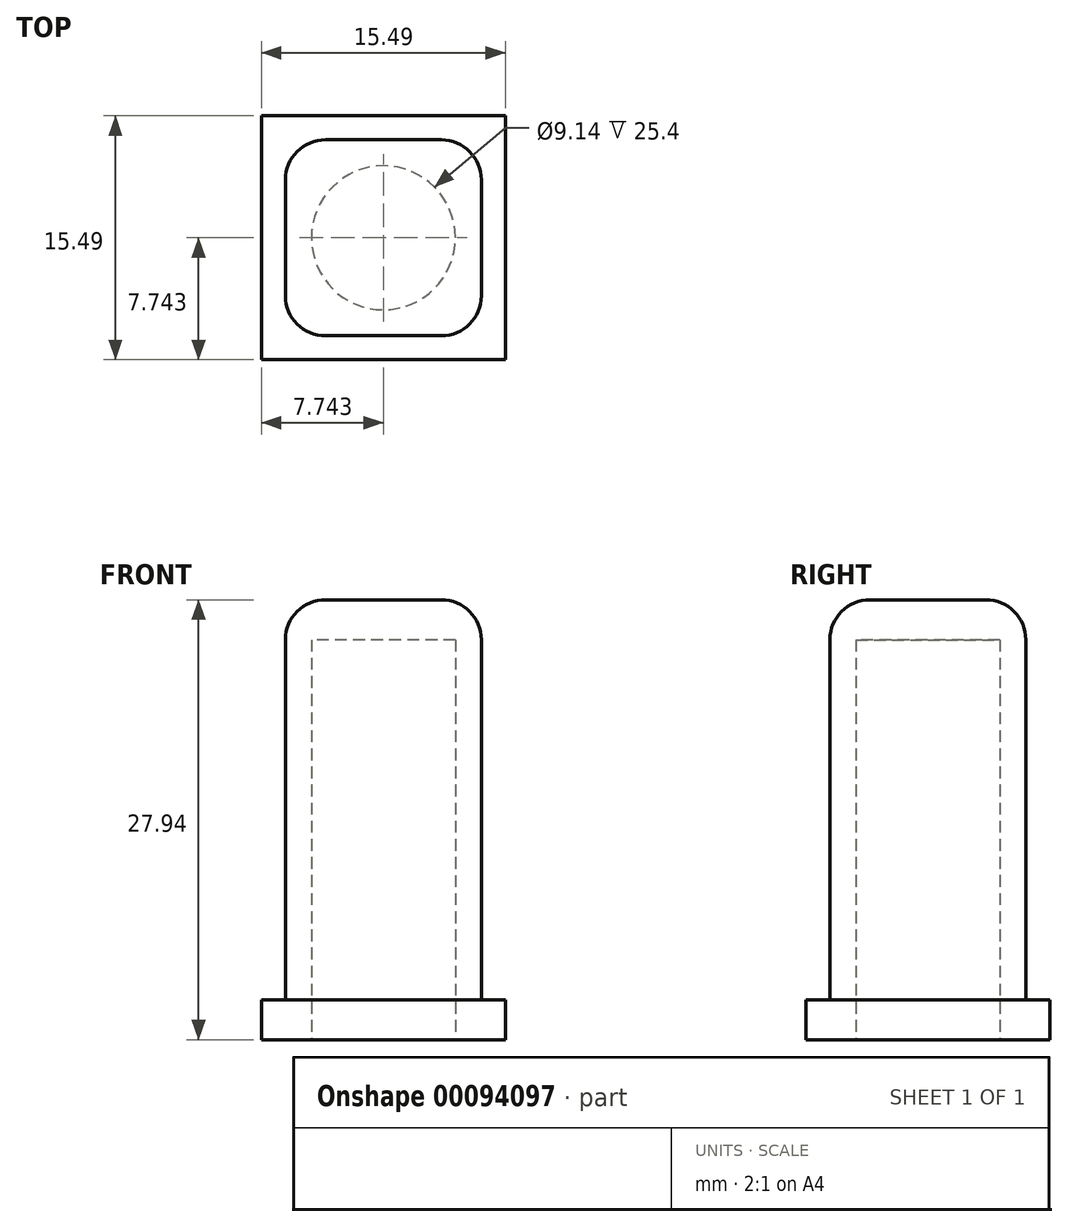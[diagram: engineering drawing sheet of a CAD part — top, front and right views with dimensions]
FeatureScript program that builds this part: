
annotation { "Feature Type Name" : "Feature", "Feature Type Description" : "" }
export const myFeature = defineFeature(function(context is Context, id is Id, definition is map)
    precondition{}
    {
        {
            var Q0;
            Q0=qCreatedBy(makeId("Top.planeOp"),FACE);
            var sketch = newSketch(context, id + "F0", { "sketchPlane" : qUnion([Q0])});
            skLineSegment(sketch, "E0.bottom", {"start": v(0, 0) * mm, "end": v(12.45, 0) * mm});
            skLineSegment(sketch, "E0.top", {"start": v(0, 12.45) * mm, "end": v(12.45, 12.45) * mm});
            skLineSegment(sketch, "E0.left", {"start": v(0, 0) * mm, "end": v(0, 12.45) * mm});
            skLineSegment(sketch, "E0.right", {"start": v(12.45, 0) * mm, "end": v(12.45, 12.45) * mm});
            skLineSegment(sketch, "E1", {"start": v(6.22, 12.45) * mm, "end": v(6.22, 0) * mm, "construction": true});
            skLineSegment(sketch, "E2", {"start": v(6.22, 0) * mm, "end": v(12.45, 6.22) * mm, "construction": true});
            skLineSegment(sketch, "E3", {"start": v(12.45, 6.22) * mm, "end": v(0, 6.22) * mm, "construction": true});
            skCircle(sketch, "E4", {"center": v(6.22, 6.22) * mm, "radius": 4.57 * mm});
            skLineSegment(sketch, "E5.0", {"start": v(-1.52, 13.97) * mm, "end": v(13.97, 13.97) * mm});
            skLineSegment(sketch, "E5.1", {"start": v(-1.52, -1.52) * mm, "end": v(-1.52, 13.97) * mm});
            skLineSegment(sketch, "E5.2", {"start": v(-1.52, -1.52) * mm, "end": v(13.97, -1.52) * mm});
            skLineSegment(sketch, "E5.3", {"start": v(13.97, -1.52) * mm, "end": v(13.97, 13.97) * mm});
            skSolve(sketch);
        }
        {
            var Q0;
            Q0=makeQuery(id+"F0.imprint","IMPRINT",FACE,{"disambiguationData":[TD([[makeQuery(id+"F0.imprint","IMPRINT",EDGE,{"derivedFrom":sQuery(id+"F0.wireOp",EDGE,"E0.bottom")}),1.0]])]});
            extrude(context, id + "F1", {"entities" : qUnion([Q0]), "depth" : 25.4 * mm, "offsetDistance" : 25.4 * mm});
        }
        {
            var Q0;
            Q0=makeQuery(id+"F0.imprint","IMPRINT",FACE,{"disambiguationData":[TD([[makeQuery(id+"F0.imprint","IMPRINT",EDGE,{"derivedFrom":sQuery(id+"F0.wireOp",EDGE,"E0.bottom")}),-1.0]])]});
            extrude(context, id + "F2", {"entities" : qUnion([Q0]), "operationType" : NewBodyOperationType.ADD, "surfaceOperationType" : NewSurfaceOperationType.ADD, "depth" : 2.54 * mm, "offsetDistance" : 25.4 * mm});
        }
        {
            var Q0;
            Q0=makeQuery(id+"F1.opExtrude","CAP_FACE",FACE,{"disambiguationData":[OSD([sQuery(id+"F0.wireOp",EDGE,"E0.bottom"),sQuery(id+"F0.wireOp",EDGE,"E0.top"),sQuery(id+"F0.wireOp",EDGE,"E0.left"),sQuery(id+"F0.wireOp",EDGE,"E0.right"),sQuery(id+"F0.wireOp",EDGE,"E4")])],"isStart":false});
            var sketch = newSketch(context, id + "F3", { "sketchPlane" : qUnion([Q0])});
            skLineSegment(sketch, "E6.0", {"start": v(0, 0) * mm, "end": v(0, 12.45) * mm});
            skLineSegment(sketch, "E7.0", {"start": v(0, 12.45) * mm, "end": v(12.45, 12.45) * mm});
            skLineSegment(sketch, "E8.0", {"start": v(12.45, 0) * mm, "end": v(12.45, 12.45) * mm});
            skLineSegment(sketch, "E9.0", {"start": v(0, 0) * mm, "end": v(12.45, 0) * mm});
            skSolve(sketch);
        }
        {
            var Q0;
            Q0=makeQuery(id+"F3.imprint","IMPRINT",FACE,{"disambiguationData":[TD([[makeQuery(id+"F3.imprint","IMPRINT",EDGE,{"derivedFrom":sQuery(id+"F3.wireOp",EDGE,"E6.0")}),-1.0]])]});
            var Q1;
            Q1=makeQuery(id+"F3.imprint","IMPRINT",FACE,{"disambiguationData":[TD([[makeQuery(id+"F3.imprint","IMPRINT",EDGE,{"derivedFrom":makeQuery(id+"F1.opExtrude","CAP_EDGE",EDGE,{"disambiguationData":[OSD([sQuery(id+"F0.wireOp",EDGE,"E4")])],"isStart":false})}),1.0]])]});
            extrude(context, id + "F4", {"entities" : qUnion([Q0, Q1]), "operationType" : NewBodyOperationType.ADD, "depth" : 2.54 * mm, "offsetDistance" : 25.4 * mm});
        }
        {
            var Q0;
            Q0=makeQuery(id+"F4.boolean.opBoolean","MERGE",EDGE,{"derivedFrom":[makeQuery(id+"F1.opExtrude","SWEPT_EDGE",EDGE,{"disambiguationData":[OSD([sQuery(id+"F0.wireOp",EDGE,"E0.top"),sQuery(id+"F0.wireOp",EDGE,"E0.left")])]}),makeQuery(id+"F4.opExtrude","SWEPT_EDGE",EDGE,{"disambiguationData":[OSD([sQuery(id+"F3.wireOp",EDGE,"E6.0"),sQuery(id+"F3.wireOp",EDGE,"E7.0")])]})]});
            var Q1;
            Q1=makeQuery(id+"F4.boolean.opBoolean","MERGE",EDGE,{"derivedFrom":[makeQuery(id+"F1.opExtrude","SWEPT_EDGE",EDGE,{"disambiguationData":[OSD([sQuery(id+"F0.wireOp",EDGE,"E0.top"),sQuery(id+"F0.wireOp",EDGE,"E0.right")])]}),makeQuery(id+"F4.opExtrude","SWEPT_EDGE",EDGE,{"disambiguationData":[OSD([sQuery(id+"F3.wireOp",EDGE,"E7.0"),sQuery(id+"F3.wireOp",EDGE,"E8.0")])]})]});
            var Q2;
            Q2=makeQuery(id+"F4.boolean.opBoolean","MERGE",EDGE,{"derivedFrom":[makeQuery(id+"F1.opExtrude","SWEPT_EDGE",EDGE,{"disambiguationData":[OSD([sQuery(id+"F0.wireOp",EDGE,"E0.bottom"),sQuery(id+"F0.wireOp",EDGE,"E0.left")])]}),makeQuery(id+"F4.opExtrude","SWEPT_EDGE",EDGE,{"disambiguationData":[OSD([sQuery(id+"F3.wireOp",EDGE,"E6.0"),sQuery(id+"F3.wireOp",EDGE,"E9.0")])]})]});
            var Q3;
            Q3=makeQuery(id+"F4.boolean.opBoolean","MERGE",EDGE,{"derivedFrom":[makeQuery(id+"F1.opExtrude","SWEPT_EDGE",EDGE,{"disambiguationData":[OSD([sQuery(id+"F0.wireOp",EDGE,"E0.bottom"),sQuery(id+"F0.wireOp",EDGE,"E0.right")])]}),makeQuery(id+"F4.opExtrude","SWEPT_EDGE",EDGE,{"disambiguationData":[OSD([sQuery(id+"F3.wireOp",EDGE,"E8.0"),sQuery(id+"F3.wireOp",EDGE,"E9.0")])]})]});
            var Q4;
            Q4=makeQuery(id+"F4.opExtrude","CAP_EDGE",EDGE,{"disambiguationData":[OSD([sQuery(id+"F3.wireOp",EDGE,"E7.0")])],"isStart":false});
            var Q5;
            Q5=makeQuery(id+"F4.opExtrude","CAP_EDGE",EDGE,{"disambiguationData":[OSD([sQuery(id+"F3.wireOp",EDGE,"E8.0")])],"isStart":false});
            var Q6;
            Q6=makeQuery(id+"F4.opExtrude","CAP_EDGE",EDGE,{"disambiguationData":[OSD([sQuery(id+"F3.wireOp",EDGE,"E9.0")])],"isStart":false});
            var Q7;
            Q7=makeQuery(id+"F4.opExtrude","CAP_EDGE",EDGE,{"disambiguationData":[OSD([sQuery(id+"F3.wireOp",EDGE,"E6.0")])],"isStart":false});
            fillet(context, id + "F5", {"entities" : qUnion([Q0, Q1, Q2, Q3, Q4, Q5, Q6, Q7]), "radius" : 2.54 * mm, "tangentPropagation" : true, "allowEdgeOverflow" : false});
        }
    });
